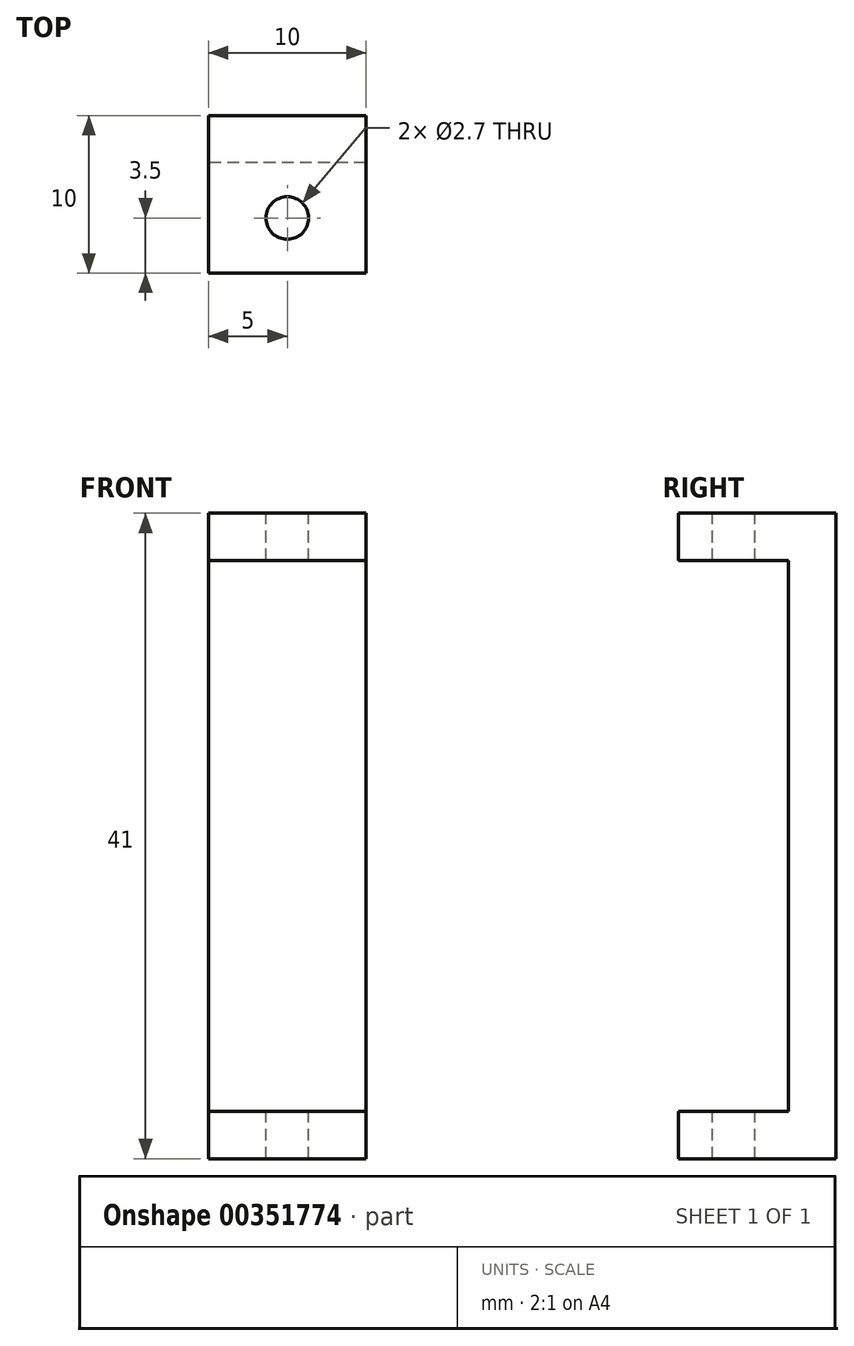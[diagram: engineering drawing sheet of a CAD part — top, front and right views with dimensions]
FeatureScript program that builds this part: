
annotation { "Feature Type Name" : "Feature", "Feature Type Description" : "" }
export const myFeature = defineFeature(function(context is Context, id is Id, definition is map)
    precondition{}
    {
        {
            var Q0;
            Q0=qCreatedBy(makeId("Top.planeOp"),FACE);
            var sketch = newSketch(context, id + "F0", { "sketchPlane" : qUnion([Q0])});
            skLineSegment(sketch, "E0.bottom", {"start": v(5, -5) * mm, "end": v(-5, -5) * mm});
            skLineSegment(sketch, "E0.top", {"start": v(5, 5) * mm, "end": v(-5, 5) * mm});
            skLineSegment(sketch, "E0.left", {"start": v(5, -5) * mm, "end": v(5, 5) * mm});
            skLineSegment(sketch, "E0.right", {"start": v(-5, -5) * mm, "end": v(-5, 5) * mm});
            skPoint(sketch, "E0.middle", {"position": v(0, 0) * mm});
            skSolve(sketch);
        }
        {
            var Q0;
            Q0 = qSketchRegion(id + "F0", true);
            var Q1;
            Q1=makeQuery(id+"F0.imprint","IMPRINT",FACE,{"disambiguationData":[TD([[makeQuery(id+"F0.imprint","IMPRINT",EDGE,{"derivedFrom":sQuery(id+"F0.wireOp",EDGE,"E0.bottom")}),-1.0]])]});
            extrude(context, id + "F1", {"entities" : qUnion([Q0, Q1]), "depth" : 41 * mm, "offsetDistance" : 25 * mm});
        }
        {
            var Q0;
            Q0=makeQuery(id+"F1.opExtrude","SWEPT_FACE",FACE,{"disambiguationData":[OSD([sQuery(id+"F0.wireOp",EDGE,"E0.bottom")])]});
            var sketch = newSketch(context, id + "F2", { "sketchPlane" : qUnion([Q0])});
            skLineSegment(sketch, "E1.bottom", {"start": v(5, 38) * mm, "end": v(-5, 38) * mm});
            skLineSegment(sketch, "E1.top", {"start": v(5, 3) * mm, "end": v(-5, 3) * mm});
            skLineSegment(sketch, "E1.left", {"start": v(5, 38) * mm, "end": v(5, 3) * mm});
            skLineSegment(sketch, "E1.right", {"start": v(-5, 38) * mm, "end": v(-5, 3) * mm});
            skSolve(sketch);
        }
        {
            var Q0;
            Q0 = qSketchRegion(id + "F2", true);
            extrude(context, id + "F3", {"entities" : qUnion([Q0]), "operationType" : NewBodyOperationType.REMOVE, "oppositeDirection" : true, "depth" : 7 * mm, "offsetDistance" : 25 * mm});
        }
        {
            var Q0;
            Q0=makeQuery(id+"F1.opExtrude","CAP_FACE",FACE,{"disambiguationData":[OSD([sQuery(id+"F0.wireOp",EDGE,"E0.bottom"),sQuery(id+"F0.wireOp",EDGE,"E0.top"),sQuery(id+"F0.wireOp",EDGE,"E0.left"),sQuery(id+"F0.wireOp",EDGE,"E0.right")])],"isStart":false});
            var sketch = newSketch(context, id + "F4", { "sketchPlane" : qUnion([Q0])});
            skCircle(sketch, "E2", {"center": v(0, -1.5) * mm, "radius": 1.35 * mm});
            skSolve(sketch);
        }
        {
            var Q0;
            Q0=makeQuery(id+"F4.imprint","IMPRINT",FACE,{"disambiguationData":[TD([[makeQuery(id+"F4.imprint","IMPRINT",EDGE,{"derivedFrom":sQuery(id+"F4.wireOp",EDGE,"E2")}),1.0]])]});
            extrude(context, id + "F5", {"entities" : qUnion([Q0]), "operationType" : NewBodyOperationType.REMOVE, "oppositeDirection" : true, "depth" : 50 * mm, "offsetDistance" : 25 * mm});
        }
    });
